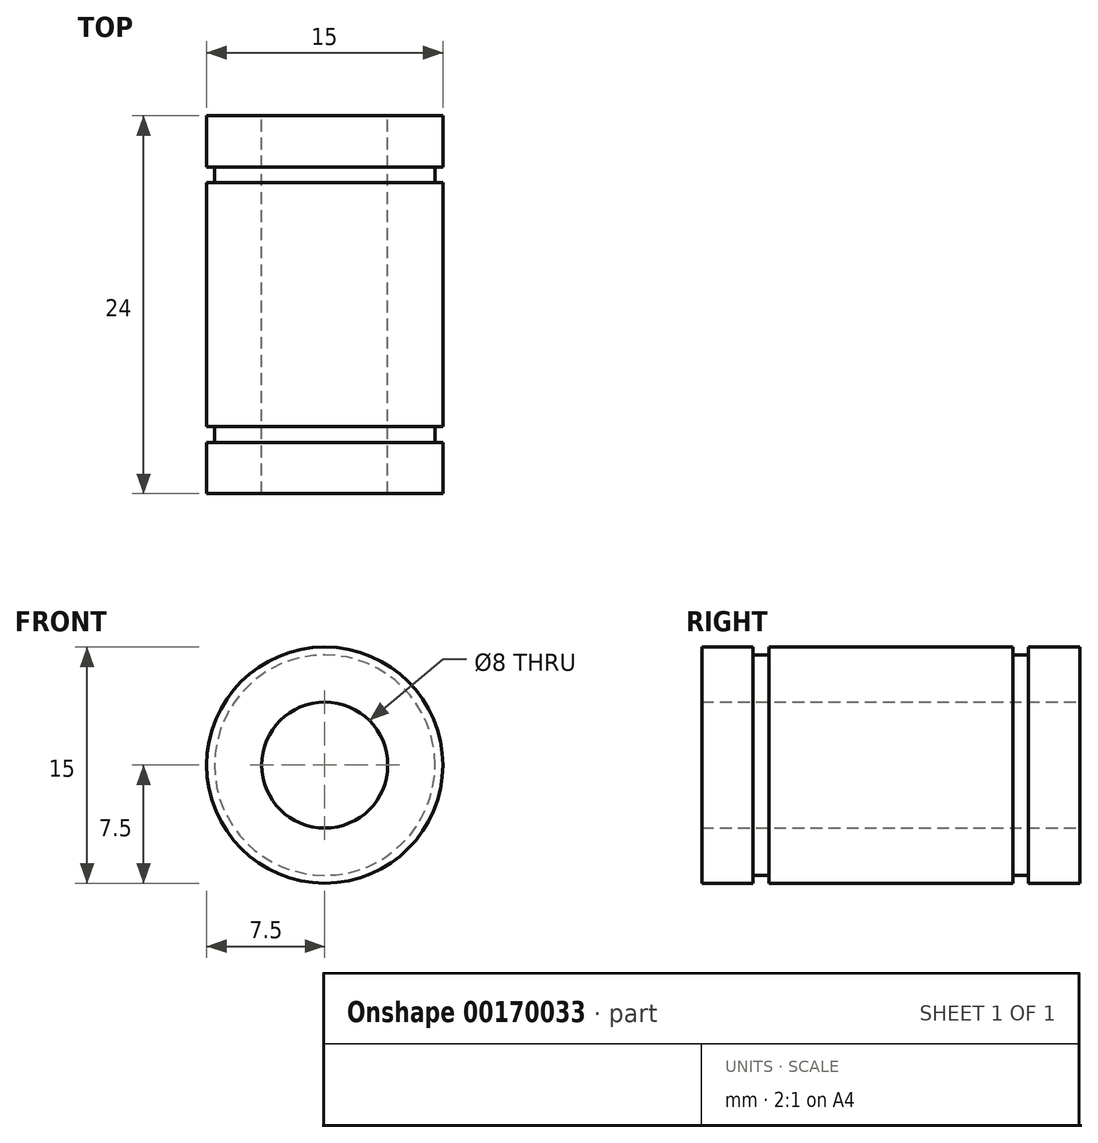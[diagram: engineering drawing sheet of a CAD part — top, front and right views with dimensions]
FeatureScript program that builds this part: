
annotation { "Feature Type Name" : "Feature", "Feature Type Description" : "" }
export const myFeature = defineFeature(function(context is Context, id is Id, definition is map)
    precondition{}
    {
        {
            var Q0;
            Q0=qCreatedBy(makeId("Front.planeOp"),FACE);
            var sketch = newSketch(context, id + "F0", { "sketchPlane" : qUnion([Q0])});
            skCircle(sketch, "E0", {"center": v(0, 0) * mm, "radius": 7.5 * mm});
            skCircle(sketch, "E1", {"center": v(0, 0) * mm, "radius": 4 * mm});
            skSolve(sketch);
        }
        {
            var Q0;
            Q0=qSketchRegion(id+"F0",true);
            extrude(context, id + "F1", {"entities" : qUnion([Q0]), "depth" : 3.25 * mm});
        }
        {
            var Q0;
            Q0=makeQuery(id+"F1.opExtrude","CAP_FACE",FACE,{"disambiguationData":[OSD([sQuery(id+"F0.wireOp",EDGE,"E0"),sQuery(id+"F0.wireOp",EDGE,"E1")])],"isStart":false});
            var sketch = newSketch(context, id + "F2", { "sketchPlane" : qUnion([Q0])});
            skCircle(sketch, "E2", {"center": v(0, 0) * mm, "radius": 7 * mm});
            skSolve(sketch);
        }
        {
            var Q0;
            Q0=makeQuery(id+"F2.imprint","IMPRINT",FACE,{"disambiguationData":[TD([[makeQuery(id+"F2.imprint","IMPRINT",EDGE,{"derivedFrom":sQuery(id+"F2.wireOp",EDGE,"E2")}),1.0]])]});
            var Q1;
            Q1=makeQuery(id+"F2.imprint","IMPRINT",FACE,{"disambiguationData":[TD([[makeQuery(id+"F2.imprint","IMPRINT",EDGE,{"derivedFrom":sQuery(id+"F2.wireOp",EDGE,"89afc66b-9a5b-46c4-a7c7-da3e920e76d60.MirrorC")}),-1.0]])]});
            extrude(context, id + "F3", {"entities" : qUnion([Q0, Q1]), "operationType" : NewBodyOperationType.ADD, "depth" : 1 * mm});
        }
        {
            var Q0;
            Q0=makeQuery(id+"F3.opExtrude","CAP_FACE",FACE,{"disambiguationData":[OSD([sQuery(id+"F0.wireOp",EDGE,"E1"),sQuery(id+"F2.wireOp",EDGE,"E2")])],"isStart":false});
            var sketch = newSketch(context, id + "F4", { "sketchPlane" : qUnion([Q0])});
            skCircle(sketch, "E3.0", {"center": v(0, 0) * mm, "radius": 7.5 * mm});
            skSolve(sketch);
        }
        {
            var Q0;
            Q0=makeQuery(id+"F4.imprint","IMPRINT",FACE,{"disambiguationData":[TD([[makeQuery(id+"F4.imprint","IMPRINT",EDGE,{"derivedFrom":makeQuery(id+"F3.opExtrude","CAP_EDGE",EDGE,{"disambiguationData":[OSD([sQuery(id+"F2.wireOp",EDGE,"E2")])],"isStart":false})}),1.0]])]});
            var Q1;
            Q1=makeQuery(id+"F4.imprint","IMPRINT",FACE,{"disambiguationData":[TD([[makeQuery(id+"F4.imprint","IMPRINT",EDGE,{"derivedFrom":sQuery(id+"F4.wireOp",EDGE,"E3.0")}),1.0]])]});
            extrude(context, id + "F5", {"entities" : qUnion([Q0, Q1]), "operationType" : NewBodyOperationType.ADD, "depth" : 15.5 * mm});
        }
        {
            var Q0;
            Q0=makeQuery(id+"F5.opExtrude","CAP_FACE",FACE,{"disambiguationData":[OSD([sQuery(id+"F0.wireOp",EDGE,"E1"),sQuery(id+"F4.wireOp",EDGE,"E3.0")])],"isStart":false});
            var sketch = newSketch(context, id + "F6", { "sketchPlane" : qUnion([Q0])});
            skCircle(sketch, "E4.0", {"center": v(0, 0) * mm, "radius": 7 * mm});
            skSolve(sketch);
        }
        {
            var Q0;
            Q0=makeQuery(id+"F6.imprint","IMPRINT",FACE,{"disambiguationData":[TD([[makeQuery(id+"F6.imprint","IMPRINT",EDGE,{"derivedFrom":sQuery(id+"F6.wireOp",EDGE,"E4.0")}),1.0]])]});
            extrude(context, id + "F7", {"entities" : qUnion([Q0]), "operationType" : NewBodyOperationType.ADD, "depth" : 1 * mm});
        }
        {
            var Q0;
            Q0=makeQuery(id+"F7.opExtrude","CAP_FACE",FACE,{"disambiguationData":[OSD([sQuery(id+"F0.wireOp",EDGE,"E1"),sQuery(id+"F6.wireOp",EDGE,"E4.0")])],"isStart":false});
            var sketch = newSketch(context, id + "F8", { "sketchPlane" : qUnion([Q0])});
            skCircle(sketch, "E5.0", {"center": v(0, 0) * mm, "radius": 7.5 * mm});
            skSolve(sketch);
        }
        {
            var Q0;
            Q0=makeQuery(id+"F8.imprint","IMPRINT",FACE,{"disambiguationData":[TD([[makeQuery(id+"F8.imprint","IMPRINT",EDGE,{"derivedFrom":sQuery(id+"F8.wireOp",EDGE,"E5.0")}),1.0]])]});
            var Q1;
            Q1=makeQuery(id+"F8.imprint","IMPRINT",FACE,{"disambiguationData":[TD([[makeQuery(id+"F8.imprint","IMPRINT",EDGE,{"derivedFrom":makeQuery(id+"F7.opExtrude","CAP_EDGE",EDGE,{"disambiguationData":[OSD([sQuery(id+"F6.wireOp",EDGE,"E4.0")])],"isStart":false})}),1.0]])]});
            extrude(context, id + "F9", {"entities" : qUnion([Q0, Q1]), "operationType" : NewBodyOperationType.ADD, "depth" : 3.25 * mm});
        }
    });
